# Revit family: 04790200
name_source: partatom
category: Plumbing Fixtures
units: mm (PartAtom-declared; Revit-internal decimal feet)

## family parameters
Always vertical = Yes
Cut with Voids When Loaded = No
OmniClass Number = 23.45.55.00
OmniClass Title = Sanitary Faucets, Wastes
Part Type = Normal
Room Calculation Point = No
Round Connector Dimension = Use Diameter
Shared = No
Work Plane-Based = No

## types (1)
- 04790200 Shower rail
    2D/3D/BIM Files URL = http://static.hansa.com
    3D View = https://static.hansa.com
    Advanced Features = Flexible length / can be shortened
    AssetType = Fixed
    BIMObjectName = 04790200
    BodyMaterial = Brass
    Brand = HANSA
    Catalog Drawing URL = http://static.hansa.com
    Category = Shower solutions
    CloseOffRating = 0
    Color = Chrome
    DN Size = 22 mm
    Default Elevation = 0 mm  [stored 0 ft]
    Diameter = 22 mm  [stored 0.0721785 ft]
    Dimension Drawing URL = http://static.hansa.com
    DurationUnit = Year
    EAN Number = 4057304009013
    ETIM Class Number = EC010140 Sliding rod
    FDV Document URL = http://www.hansa.com
    FaucetMainMaterial = Brass
    Finish = Polished
    FlowCoefficient = 0
    Group = Shower rail
    IfcExportAs = IfcValveType
    IfcExportType = FAUCET
    Installation Type = Wall mounted
    Installation and Maintenance Guide URL = http://static.hansa.com
    Interactive AR View URL = https://static.hansa.com
    Manufacturer = HANSA
    ManufacturerName = HANSA
    ManufacturerURL = http://www.hansa.com
    Market = International;Germany;Austria;Belgium;Netherlands;France;Czech Republic;Slovakia;Italy;Spain
    Mechanical Parts = Fixing Set
    Mobile Product Information URL = http://mpi.hansa.com
    Model = 04790200 Shower rail
    ModelReference = 04790200
    NBSDescription = Shower mixers
    NBSReference = 45-35-70/335
    Name = 04790200 Shower rail
    Name_en = 04790200 Shower rail
    NominalDepth = 103 mm
    NominalHeight = 1010 mm  [stored 3.31365 ft]
    NominalWidth = 67 mm
    Product Code = 04790200
    Product Family = HANSAACTIVEJET
    Product Image URL = http://static.hansa.com
    Product URL = http://static.hansa.com
    Sales Package dimensions (LxWxH) = 1031 x 156 x 74
    Shape = Sculptured
    Shower Parts = Shower rail;Variable fixing points;Adjustable shower rail bracket
    Size = 65x105x1010 mm
    Spare-Part Information URL = http://static.hansa.com
    Surface treatment = Chrome
    Technical DataSheet URL = http://www.hansa.com
    UNSPSC Class Number = 30181503 Showers
    URL Declaration Of Performance (DOP) = http://static.hansa.com
    URL Declaration of Asbestos = http://static.hansa.com
    URL Declaration of Conformity = http://static.hansa.com
    URL Declaration of SCIP = http://static.hansa.com
    URL EU Packaging Declaration = http://static.hansa.com
    URL EcoLabel Declaration = http://static.hansa.com
    URL REACH = http://static.hansa.com
    Uniclass2 = Pr_40_30_96_78
    Uniclass2015Description = Shower manual water supply sets
    Uniclass2015Reference = Pr_40_20_87_78
    Version = 1
    VersionDate = 01/06/2023
    Warranty Information URL = http://warranty.hansa.com
    WarrantyDescription = http://warranty.hansa.com
    WarrantyDurationUnit = Year

note: [stored X ft] marks values corroborated as IEEE doubles in the binary element streams (Revit-internal decimal feet)

## geometry (parser evidence)
native form markers: Sweep x4
no freeform markers — native parametric forms only
